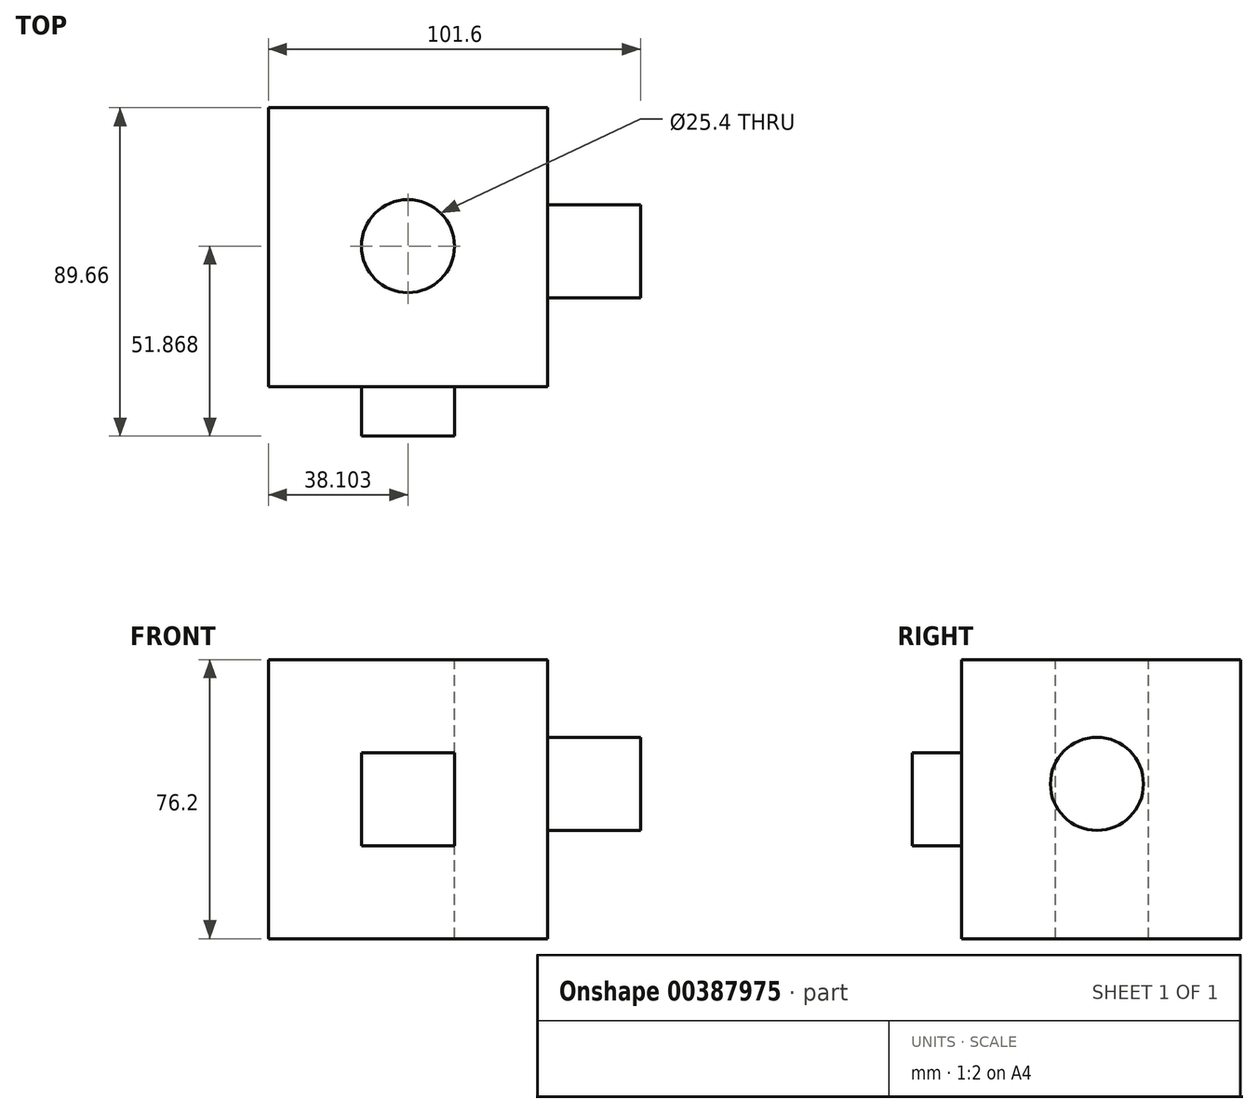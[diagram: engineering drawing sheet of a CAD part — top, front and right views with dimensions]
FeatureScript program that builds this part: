
annotation { "Feature Type Name" : "Feature", "Feature Type Description" : "" }
export const myFeature = defineFeature(function(context is Context, id is Id, definition is map)
    precondition{}
    {
        {
            var Q0;
            Q0=qCreatedBy(makeId("Front.planeOp"),FACE);
            var sketch = newSketch(context, id + "F0", { "sketchPlane" : qUnion([Q0])});
            skLineSegment(sketch, "E0.bottom", {"start": v(-111.9, -67.58) * mm, "end": v(-35.7, -67.58) * mm});
            skLineSegment(sketch, "E0.top", {"start": v(-111.9, 8.62) * mm, "end": v(-35.7, 8.62) * mm});
            skLineSegment(sketch, "E0.left", {"start": v(-111.9, -67.58) * mm, "end": v(-111.9, 8.62) * mm});
            skLineSegment(sketch, "E0.right", {"start": v(-35.7, -67.58) * mm, "end": v(-35.7, 8.62) * mm});
            skSolve(sketch);
        }
        {
            var Q0;
            Q0=makeQuery(id+"F0.imprint","IMPRINT",FACE,{"disambiguationData":[TD([[makeQuery(id+"F0.imprint","IMPRINT",EDGE,{"derivedFrom":sQuery(id+"F0.wireOp",EDGE,"E0.bottom")}),1.0]])]});
            extrude(context, id + "F1", {"entities" : qUnion([Q0]), "depth" : 76.2 * mm});
        }
        {
            var Q0;
            Q0=makeQuery(id+"F1.opExtrude","SWEPT_FACE",FACE,{"disambiguationData":[OSD([sQuery(id+"F0.wireOp",EDGE,"E0.top")])]});
            var sketch = newSketch(context, id + "F2", { "sketchPlane" : qUnion([Q0])});
            skPoint(sketch, "E1", {"position": v(-73.8, -37.8) * mm});
            skSolve(sketch);
        }
        {
            var Q0;
            Q0=sQuery(id+"F2.wireOp",VERTEX,"E1");
            var Q1;
            Q1=makeQuery(id+"F1.opExtrude","SWEPT_BODY",BODY,{"disambiguationData":[OSD([sQuery(id+"F0.wireOp",EDGE,"E0.bottom"),sQuery(id+"F0.wireOp",EDGE,"E0.top"),sQuery(id+"F0.wireOp",EDGE,"E0.left"),sQuery(id+"F0.wireOp",EDGE,"E0.right")])]});
            hole(context, id + "F3", {"style" : HoleStyle.SIMPLE, "endStyle" : HoleEndStyle.THROUGH, "holeDiameter" : 25.4 * mm, "isTappedThrough" : true, "tappedDepth" : 12.7 * mm, "tapClearance" : 3, "locations" : qUnion([Q0]), "scope" : qUnion([Q1])});
        }
        {
            var Q0;
            Q0=makeQuery(id+"F1.opExtrude","CAP_FACE",FACE,{"disambiguationData":[OSD([sQuery(id+"F0.wireOp",EDGE,"E0.bottom"),sQuery(id+"F0.wireOp",EDGE,"E0.top"),sQuery(id+"F0.wireOp",EDGE,"E0.left"),sQuery(id+"F0.wireOp",EDGE,"E0.right")])],"isStart":false});
            var sketch = newSketch(context, id + "F4", { "sketchPlane" : qUnion([Q0])});
            skLineSegment(sketch, "E2.bottom", {"start": v(-86.5, -42.18) * mm, "end": v(-61.1, -42.18) * mm});
            skLineSegment(sketch, "E2.top", {"start": v(-86.5, -16.78) * mm, "end": v(-61.1, -16.78) * mm});
            skLineSegment(sketch, "E2.left", {"start": v(-86.5, -42.18) * mm, "end": v(-86.5, -16.78) * mm});
            skLineSegment(sketch, "E2.right", {"start": v(-61.1, -42.18) * mm, "end": v(-61.1, -16.78) * mm});
            skSolve(sketch);
        }
        {
            var Q0;
            Q0=makeQuery(id+"F4.imprint","IMPRINT",FACE,{"disambiguationData":[TD([[makeQuery(id+"F4.imprint","IMPRINT",EDGE,{"derivedFrom":sQuery(id+"F4.wireOp",EDGE,"E2.bottom")}),1.0]])]});
            extrude(context, id + "F5", {"entities" : qUnion([Q0]), "operationType" : NewBodyOperationType.ADD, "depth" : 13.46 * mm});
        }
        {
            var Q0;
            Q0=makeQuery(id+"F1.opExtrude","SWEPT_FACE",FACE,{"disambiguationData":[OSD([sQuery(id+"F0.wireOp",EDGE,"E0.right")])]});
            var sketch = newSketch(context, id + "F6", { "sketchPlane" : qUnion([Q0])});
            skCircle(sketch, "E3", {"center": v(-39.24, -25.31) * mm, "radius": 12.7 * mm});
            skSolve(sketch);
        }
        {
            var Q0;
            Q0=makeQuery(id+"F6.imprint","IMPRINT",FACE,{"disambiguationData":[TD([[makeQuery(id+"F6.imprint","IMPRINT",EDGE,{"derivedFrom":sQuery(id+"F6.wireOp",EDGE,"E3")}),1.0]])]});
            extrude(context, id + "F7", {"entities" : qUnion([Q0]), "operationType" : NewBodyOperationType.ADD, "depth" : 25.4 * mm});
        }
        {
            var Q0;
            Q0=makeQuery(id+"F6.imprint","IMPRINT",FACE,{"disambiguationData":[TD([[makeQuery(id+"F6.imprint","IMPRINT",EDGE,{"derivedFrom":sQuery(id+"F6.wireOp",EDGE,"E3")}),1.0]])]});
            extrude(context, id + "F8", {"entities" : qUnion([Q0]), "operationType" : NewBodyOperationType.ADD, "depth" : 25.4 * mm});
        }
    });
